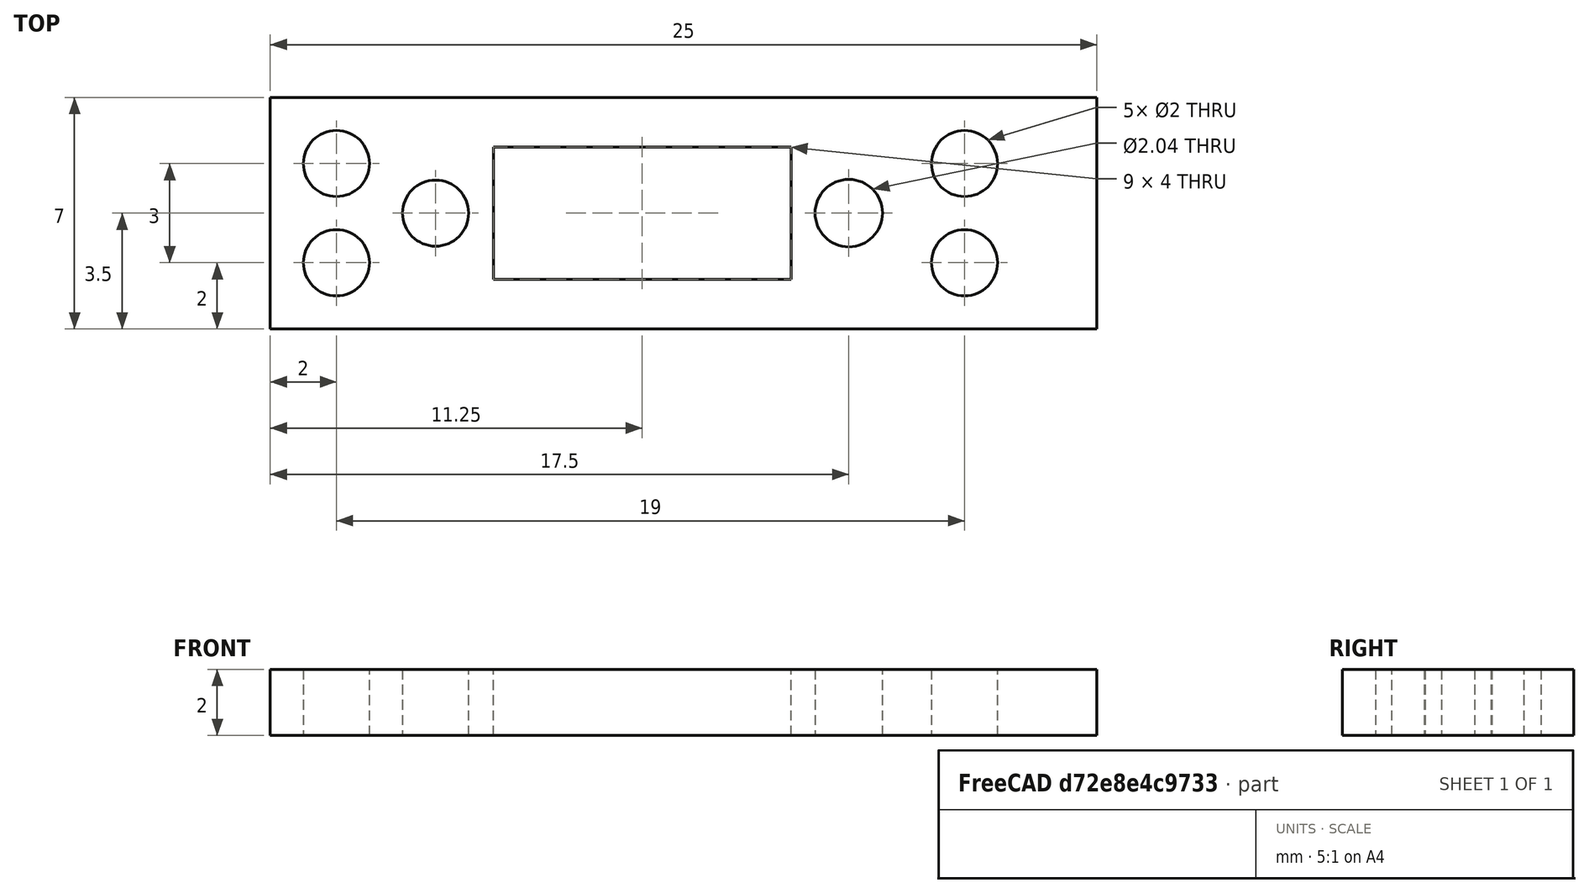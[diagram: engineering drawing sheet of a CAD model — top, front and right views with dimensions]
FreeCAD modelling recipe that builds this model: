
FCSTD DOCUMENT  (FreeCAD 0.19R)
Label: bracket-nondimensional
License: All rights reserved
LicenseURL: http://en.wikipedia.org/wiki/All_rights_reserved
objects: Part::Cut×7, Part::Cylinder×6, Part::Box×2
note: 15 computed .brp shape members not serialized (recipe doc carries the construction recipe); baked Part::Feature solids carry a one-line shape summary decoded from their .brp

FEATURE [Part::Box] Box  label="Cube"
  AttacherType = Attacher::AttachEngine3D
  Height = 2
  Length = 25
  Placement = pos=(-5,0,0) rot=(0,0,1;0rad)
  Width = 7
FEATURE [Part::Box] Box001  label="Cube001"
  AttacherType = Attacher::AttachEngine3D
  Height = 2
  Length = 9
  Placement = pos=(1.75,1.5,0) rot=(0,0,1;0rad)
  Width = 4
FEATURE [Part::Cut] Cut
  Base = -> Box
  Tool = -> Box001
FEATURE [Part::Cylinder] Cylinder
  Angle = 360
  AttacherType = Attacher::AttachEngine3D
  Height = 2
  Placement = pos=(12.5,3.5,0) rot=(0,0,1;0rad)
  Radius = 1.02
FEATURE [Part::Cut] Cut001
  Base = -> Cut
  Tool = -> Cylinder
FEATURE [Part::Cylinder] Cylinder001
  Angle = 360
  AttacherType = Attacher::AttachEngine3D
  Height = 2
  Placement = pos=(0,3.5,0) rot=(0,0,1;0rad)
  Radius = 1
FEATURE [Part::Cut] Cut002
  Base = -> Cut001
  Tool = -> Cylinder001
FEATURE [Part::Cylinder] Cylinder002
  Angle = 360
  AttacherType = Attacher::AttachEngine3D
  Height = 2
  Placement = pos=(-3,5,0) rot=(0,0,1;0rad)
  Radius = 1
FEATURE [Part::Cylinder] Cylinder003
  Angle = 360
  AttacherType = Attacher::AttachEngine3D
  Height = 2
  Placement = pos=(-3,2,0) rot=(0,0,1;0rad)
  Radius = 1
FEATURE [Part::Cut] Cut003
  Base = -> Cut002
  Tool = -> Cylinder002
FEATURE [Part::Cut] Cut004
  Base = -> Cut003
  Tool = -> Cylinder003
FEATURE [Part::Cylinder] Cylinder004
  Angle = 360
  AttacherType = Attacher::AttachEngine3D
  Height = 2
  Placement = pos=(16,2,0) rot=(0,0,1;0rad)
  Radius = 1
FEATURE [Part::Cut] Cut005
  Base = -> Cut004
  Tool = -> Cylinder004
FEATURE [Part::Cylinder] Cylinder005
  Angle = 360
  AttacherType = Attacher::AttachEngine3D
  Height = 2
  Placement = pos=(16,5,0) rot=(0,0,1;0rad)
  Radius = 1
FEATURE [Part::Cut] Cut006
  Base = -> Cut005
  Tool = -> Cylinder005
